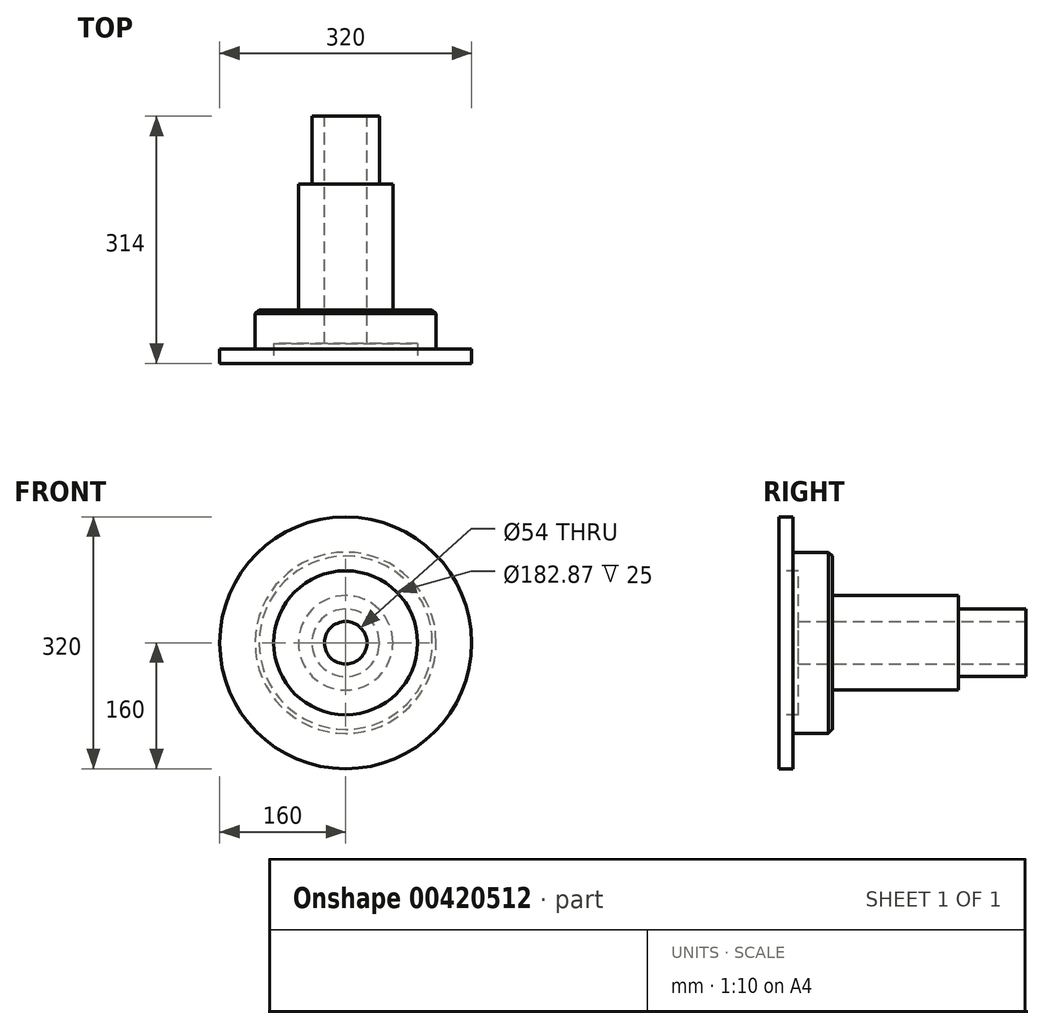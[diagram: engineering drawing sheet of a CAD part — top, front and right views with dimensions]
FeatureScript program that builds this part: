
annotation { "Feature Type Name" : "Feature", "Feature Type Description" : "" }
export const myFeature = defineFeature(function(context is Context, id is Id, definition is map)
    precondition{}
    {
        {
            var Q0;
            Q0=qCreatedBy(makeId("Front.planeOp"),FACE);
            var sketch = newSketch(context, id + "F0", { "sketchPlane" : qUnion([Q0])});
            skCircle(sketch, "E0", {"center": v(0, 0) * mm, "radius": 60 * mm});
            skSolve(sketch);
        }
        {
            var Q0;
            Q0=qSketchRegion(id+"F0",true);
            extrude(context, id + "F1", {"entities" : qUnion([Q0]), "depth" : 160 * mm});
        }
        {
            var Q0;
            Q0=makeQuery(id+"F1.opExtrude","CAP_FACE",FACE,{"disambiguationData":[OSD([sQuery(id+"F0.wireOp",EDGE,"E0")])],"isStart":false});
            var sketch = newSketch(context, id + "F2", { "sketchPlane" : qUnion([Q0])});
            skCircle(sketch, "E1", {"center": v(0, 0) * mm, "radius": 115 * mm});
            skSolve(sketch);
        }
        {
            var Q0;
            Q0=qSketchRegion(id+"F2",true);
            extrude(context, id + "F3", {"entities" : qUnion([Q0]), "operationType" : NewBodyOperationType.ADD, "depth" : 50 * mm});
        }
        {
            var Q0;
            Q0=makeQuery(id+"F3.opExtrude","CAP_FACE",FACE,{"disambiguationData":[OSD([sQuery(id+"F2.wireOp",EDGE,"E1")])],"isStart":false});
            var sketch = newSketch(context, id + "F4", { "sketchPlane" : qUnion([Q0])});
            skCircle(sketch, "E2", {"center": v(0, 0) * mm, "radius": 160 * mm});
            skSolve(sketch);
        }
        {
            var Q0;
            Q0=qSketchRegion(id+"F4",true);
            extrude(context, id + "F5", {"entities" : qUnion([Q0]), "operationType" : NewBodyOperationType.ADD, "depth" : 18 * mm});
        }
        {
            var Q0;
            Q0=makeQuery(id+"F3.opExtrude","CAP_EDGE",EDGE,{"disambiguationData":[OSD([sQuery(id+"F2.wireOp",EDGE,"E1")])],"isStart":true});
            chamfer(context, id + "F6", {"entities" : qUnion([Q0]), "width" : 5 * mm, "tangentPropagation" : true});
        }
        {
            var Q0;
            Q0=makeQuery(id+"F1.opExtrude","CAP_FACE",FACE,{"disambiguationData":[OSD([sQuery(id+"F0.wireOp",EDGE,"E0")])],"isStart":true});
            var sketch = newSketch(context, id + "F7", { "sketchPlane" : qUnion([Q0])});
            skCircle(sketch, "E3", {"center": v(0, 0) * mm, "radius": 42.88 * mm});
            skSolve(sketch);
        }
        {
            var Q0;
            Q0=qSketchRegion(id+"F7",true);
            extrude(context, id + "F8", {"entities" : qUnion([Q0]), "operationType" : NewBodyOperationType.ADD, "depth" : 86 * mm});
        }
        {
            var Q0;
            Q0=makeQuery(id+"F8.opExtrude","CAP_FACE",FACE,{"disambiguationData":[OSD([sQuery(id+"F7.wireOp",EDGE,"E3")])],"isStart":false});
            var sketch = newSketch(context, id + "F9", { "sketchPlane" : qUnion([Q0])});
            skCircle(sketch, "E4", {"center": v(0, 0) * mm, "radius": 27 * mm});
            skSolve(sketch);
        }
        {
            var Q0;
            Q0=qSketchRegion(id+"F9",true);
            extrude(context, id + "F10", {"entities" : qUnion([Q0]), "operationType" : NewBodyOperationType.REMOVE, "oppositeDirection" : true, "depth" : 430 * mm});
        }
        {
            var Q0;
            Q0=makeQuery(id+"F5.opExtrude","CAP_FACE",FACE,{"disambiguationData":[OSD([sQuery(id+"F4.wireOp",EDGE,"E2")])],"isStart":false});
            var sketch = newSketch(context, id + "F11", { "sketchPlane" : qUnion([Q0])});
            skCircle(sketch, "E5", {"center": v(0, 0) * mm, "radius": 91.44 * mm});
            skSolve(sketch);
        }
        {
            var Q0;
            Q0 = qSketchRegion(id + "F11", true);
            extrude(context, id + "F12", {"entities" : qUnion([Q0]), "operationType" : NewBodyOperationType.REMOVE, "oppositeDirection" : true, "depth" : 25 * mm});
        }
    });
